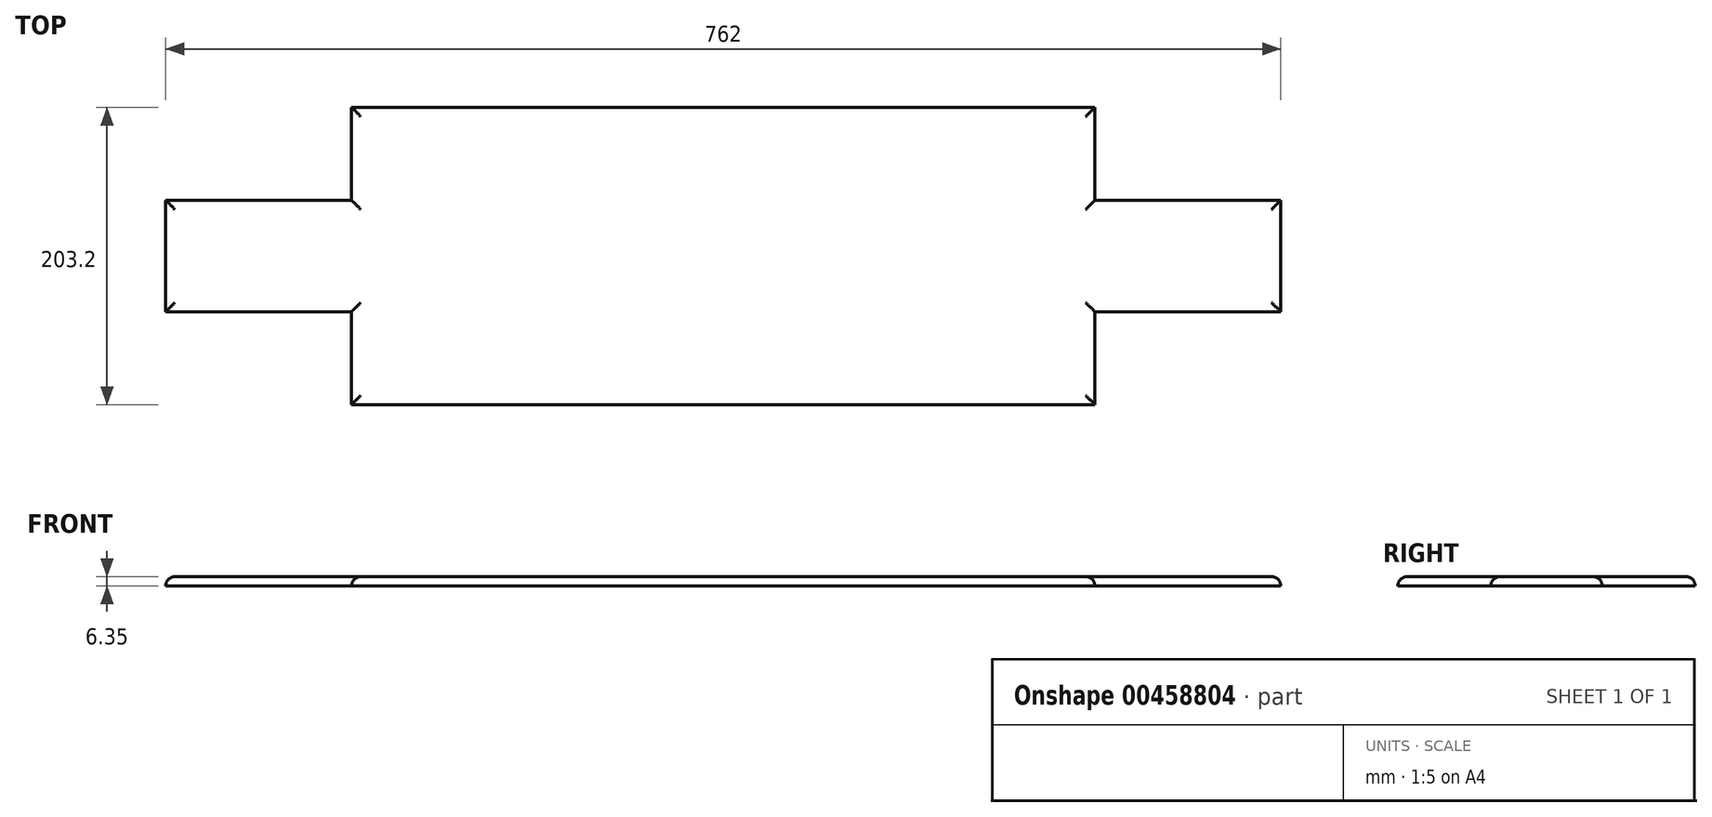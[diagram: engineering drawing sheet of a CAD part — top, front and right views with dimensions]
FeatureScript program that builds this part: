
annotation { "Feature Type Name" : "Feature", "Feature Type Description" : "" }
export const myFeature = defineFeature(function(context is Context, id is Id, definition is map)
    precondition{}
    {
        {
            var Q0;
            Q0=qCreatedBy(makeId("Top.planeOp"),FACE);
            var sketch = newSketch(context, id + "F0", { "sketchPlane" : qUnion([Q0])});
            skLineSegment(sketch, "E0.bottom", {"start": v(381, 101.6) * mm, "end": v(-381, 101.6) * mm});
            skLineSegment(sketch, "E0.top", {"start": v(381, -101.6) * mm, "end": v(-381, -101.6) * mm});
            skLineSegment(sketch, "E0.left", {"start": v(381, 101.6) * mm, "end": v(381, -101.6) * mm});
            skLineSegment(sketch, "E0.right", {"start": v(-381, 101.6) * mm, "end": v(-381, -101.6) * mm});
            skPoint(sketch, "E0.middle", {"position": v(0, 0) * mm});
            skSolve(sketch);
        }
        {
            var Q0;
            Q0=makeQuery(id+"F0.imprint","IMPRINT",FACE,{"disambiguationData":[TD([[makeQuery(id+"F0.imprint","IMPRINT",EDGE,{"derivedFrom":sQuery(id+"F0.wireOp",EDGE,"E0.bottom")}),1.0]])]});
            extrude(context, id + "F1", {"entities" : qUnion([Q0]), "depth" : 6.35 * mm});
        }
        {
            var Q0;
            Q0=makeQuery(id+"F1.opExtrude","CAP_FACE",FACE,{"disambiguationData":[OSD([sQuery(id+"F0.wireOp",EDGE,"E0.bottom"),sQuery(id+"F0.wireOp",EDGE,"E0.top"),sQuery(id+"F0.wireOp",EDGE,"E0.left"),sQuery(id+"F0.wireOp",EDGE,"E0.right")])],"isStart":false});
            var sketch = newSketch(context, id + "F2", { "sketchPlane" : qUnion([Q0])});
            skLineSegment(sketch, "E1.bottom", {"start": v(381, 101.6) * mm, "end": v(254, 101.6) * mm});
            skLineSegment(sketch, "E1.top", {"start": v(381, 38.1) * mm, "end": v(254, 38.1) * mm});
            skLineSegment(sketch, "E1.left", {"start": v(381, 101.6) * mm, "end": v(381, 38.1) * mm});
            skLineSegment(sketch, "E1.right", {"start": v(254, 101.6) * mm, "end": v(254, 38.1) * mm});
            skLineSegment(sketch, "E2.bottom", {"start": v(381, -101.6) * mm, "end": v(254, -101.6) * mm});
            skLineSegment(sketch, "E2.top", {"start": v(381, -38.1) * mm, "end": v(254, -38.1) * mm});
            skLineSegment(sketch, "E2.left", {"start": v(381, -101.6) * mm, "end": v(381, -38.1) * mm});
            skLineSegment(sketch, "E2.right", {"start": v(254, -101.6) * mm, "end": v(254, -38.1) * mm});
            skSolve(sketch);
        }
        {
            var Q0;
            Q0=makeQuery(id+"F2.imprint","IMPRINT",FACE,{"disambiguationData":[TD([[makeQuery(id+"F2.imprint","IMPRINT",EDGE,{"derivedFrom":sQuery(id+"F2.wireOp",EDGE,"E1.bottom")}),1.0]])]});
            extrude(context, id + "F3", {"entities" : qUnion([Q0]), "operationType" : NewBodyOperationType.REMOVE, "oppositeDirection" : true, "depth" : 25.4 * mm});
        }
        {
            var Q0;
            Q0=makeQuery(id+"F1.opExtrude","CAP_FACE",FACE,{"disambiguationData":[OSD([sQuery(id+"F0.wireOp",EDGE,"E0.bottom"),sQuery(id+"F0.wireOp",EDGE,"E0.top"),sQuery(id+"F0.wireOp",EDGE,"E0.left"),sQuery(id+"F0.wireOp",EDGE,"E0.right")])],"isStart":false});
            var sketch = newSketch(context, id + "F4", { "sketchPlane" : qUnion([Q0])});
            skLineSegment(sketch, "E3.bottom", {"start": v(381, -101.6) * mm, "end": v(254, -101.6) * mm});
            skLineSegment(sketch, "E3.top", {"start": v(381, -38.1) * mm, "end": v(254, -38.1) * mm});
            skLineSegment(sketch, "E3.left", {"start": v(381, -101.6) * mm, "end": v(381, -38.1) * mm});
            skLineSegment(sketch, "E3.right", {"start": v(254, -101.6) * mm, "end": v(254, -38.1) * mm});
            skSolve(sketch);
        }
        {
            var Q0;
            Q0=makeQuery(id+"F4.imprint","IMPRINT",FACE,{"disambiguationData":[TD([[makeQuery(id+"F4.imprint","IMPRINT",EDGE,{"derivedFrom":sQuery(id+"F4.wireOp",EDGE,"E3.bottom")}),-1.0]])]});
            extrude(context, id + "F5", {"entities" : qUnion([Q0]), "operationType" : NewBodyOperationType.REMOVE, "oppositeDirection" : true, "depth" : 25.4 * mm});
        }
        {
            var Q0;
            Q0=makeQuery(id+"F1.opExtrude","CAP_FACE",FACE,{"disambiguationData":[OSD([sQuery(id+"F0.wireOp",EDGE,"E0.bottom"),sQuery(id+"F0.wireOp",EDGE,"E0.top"),sQuery(id+"F0.wireOp",EDGE,"E0.left"),sQuery(id+"F0.wireOp",EDGE,"E0.right")])],"isStart":false});
            var sketch = newSketch(context, id + "F6", { "sketchPlane" : qUnion([Q0])});
            skLineSegment(sketch, "E4.bottom", {"start": v(-381, 101.6) * mm, "end": v(-254, 101.6) * mm});
            skLineSegment(sketch, "E4.top", {"start": v(-381, 38.1) * mm, "end": v(-254, 38.1) * mm});
            skLineSegment(sketch, "E4.left", {"start": v(-381, 101.6) * mm, "end": v(-381, 38.1) * mm});
            skLineSegment(sketch, "E4.right", {"start": v(-254, 101.6) * mm, "end": v(-254, 38.1) * mm});
            skSolve(sketch);
        }
        {
            var Q0;
            Q0=makeQuery(id+"F6.imprint","IMPRINT",FACE,{"disambiguationData":[TD([[makeQuery(id+"F6.imprint","IMPRINT",EDGE,{"derivedFrom":sQuery(id+"F6.wireOp",EDGE,"E4.bottom")}),1.0]])]});
            extrude(context, id + "F7", {"entities" : qUnion([Q0]), "operationType" : NewBodyOperationType.REMOVE, "oppositeDirection" : true, "depth" : 25.4 * mm});
        }
        {
            var Q0;
            Q0=makeQuery(id+"F1.opExtrude","CAP_FACE",FACE,{"disambiguationData":[OSD([sQuery(id+"F0.wireOp",EDGE,"E0.bottom"),sQuery(id+"F0.wireOp",EDGE,"E0.top"),sQuery(id+"F0.wireOp",EDGE,"E0.left"),sQuery(id+"F0.wireOp",EDGE,"E0.right")])],"isStart":false});
            var sketch = newSketch(context, id + "F8", { "sketchPlane" : qUnion([Q0])});
            skLineSegment(sketch, "E5.bottom", {"start": v(-381, -101.6) * mm, "end": v(-254, -101.6) * mm});
            skLineSegment(sketch, "E5.top", {"start": v(-381, -38.1) * mm, "end": v(-254, -38.1) * mm});
            skLineSegment(sketch, "E5.left", {"start": v(-381, -101.6) * mm, "end": v(-381, -38.1) * mm});
            skLineSegment(sketch, "E5.right", {"start": v(-254, -101.6) * mm, "end": v(-254, -38.1) * mm});
            skSolve(sketch);
        }
        {
            var Q0;
            Q0=makeQuery(id+"F8.imprint","IMPRINT",FACE,{"disambiguationData":[TD([[makeQuery(id+"F8.imprint","IMPRINT",EDGE,{"derivedFrom":sQuery(id+"F8.wireOp",EDGE,"E5.bottom")}),-1.0]])]});
            extrude(context, id + "F9", {"entities" : qUnion([Q0]), "operationType" : NewBodyOperationType.REMOVE, "oppositeDirection" : true, "depth" : 25.4 * mm});
        }
        {
            var Q0;
            Q0=makeQuery(id+"F1.opExtrude","CAP_FACE",FACE,{"disambiguationData":[OSD([sQuery(id+"F0.wireOp",EDGE,"E0.bottom"),sQuery(id+"F0.wireOp",EDGE,"E0.top"),sQuery(id+"F0.wireOp",EDGE,"E0.left"),sQuery(id+"F0.wireOp",EDGE,"E0.right")])],"isStart":false});
            fillet(context, id + "F10", {"entities" : qUnion([Q0]), "radius" : 6.35 * mm, "tangentPropagation" : true, "allowEdgeOverflow" : false});
        }
    });
